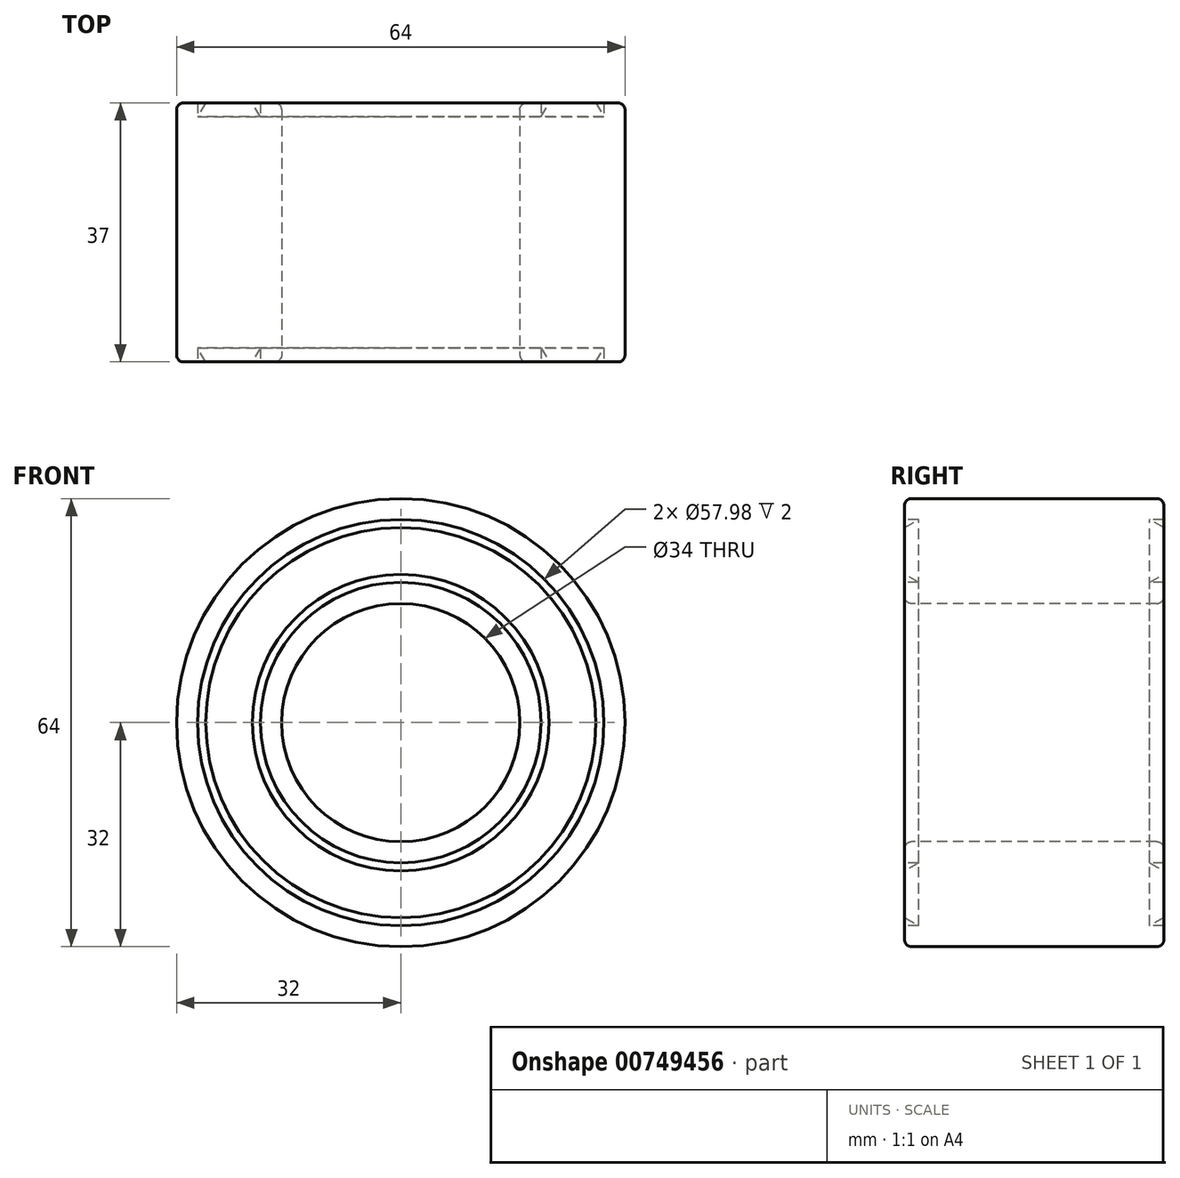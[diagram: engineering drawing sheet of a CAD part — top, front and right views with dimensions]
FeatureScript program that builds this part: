
annotation { "Feature Type Name" : "Feature", "Feature Type Description" : "" }
export const myFeature = defineFeature(function(context is Context, id is Id, definition is map)
    precondition{}
    {
        {
            var Q0;
            Q0=qCreatedBy(makeId("Right.planeOp"),FACE);
            var sketch = newSketch(context, id + "F0", { "sketchPlane" : qUnion([Q0])});
            skLineSegment(sketch, "E0", {"start": v(0, 17) * mm, "end": v(0, 20.03) * mm});
            skLineSegment(sketch, "E1", {"start": v(0, 20.03) * mm, "end": v(2, 20.03) * mm});
            skLineSegment(sketch, "E2", {"start": v(2, 20.03) * mm, "end": v(0, 21.18) * mm});
            skLineSegment(sketch, "E3", {"start": v(0, 21.18) * mm, "end": v(0, 27.83) * mm});
            skLineSegment(sketch, "E4", {"start": v(0, 27.83) * mm, "end": v(2, 28.99) * mm});
            skLineSegment(sketch, "E5", {"start": v(2, 28.99) * mm, "end": v(0, 28.99) * mm});
            skLineSegment(sketch, "E6", {"start": v(0, 28.99) * mm, "end": v(0, 32) * mm});
            skLineSegment(sketch, "E7", {"start": v(0, 32) * mm, "end": v(18.5, 32) * mm});
            skLineSegment(sketch, "E8", {"start": v(0, 17) * mm, "end": v(18.5, 17) * mm});
            skLineSegment(sketch, "E9", {"start": v(18.5, 17) * mm, "end": v(18.5, 32) * mm, "construction": true});
            skLineSegment(sketch, "E10.MirrorCS", {"start": v(37, 32) * mm, "end": v(18.5, 32) * mm});
            skLineSegment(sketch, "E11.MirrorCS", {"start": v(37, 28.99) * mm, "end": v(37, 32) * mm});
            skLineSegment(sketch, "E12.MirrorCS", {"start": v(35, 28.99) * mm, "end": v(37, 28.99) * mm});
            skLineSegment(sketch, "E13.MirrorCS", {"start": v(37, 27.83) * mm, "end": v(35, 28.99) * mm});
            skLineSegment(sketch, "E14.MirrorCS", {"start": v(37, 21.18) * mm, "end": v(37, 27.83) * mm});
            skLineSegment(sketch, "E15.MirrorCS", {"start": v(35, 20.03) * mm, "end": v(37, 21.18) * mm});
            skLineSegment(sketch, "E16.MirrorCS", {"start": v(37, 20.03) * mm, "end": v(35, 20.03) * mm});
            skLineSegment(sketch, "E17.MirrorCS", {"start": v(37, 17) * mm, "end": v(37, 20.03) * mm});
            skLineSegment(sketch, "E18.MirrorCS", {"start": v(37, 17) * mm, "end": v(18.5, 17) * mm});
            skLineSegment(sketch, "E19", {"start": v(0, 0) * mm, "end": v(4.54, 0) * mm, "construction": true});
            skSolve(sketch);
        }
        {
            var Q0;
            Q0 = qSketchRegion(id + "F0", true);
            var Q1;
            Q1=sQuery(id+"F0.wireOp",EDGE,"E19");
            revolve(context, id + "F1", {"surfaceOperationType" : NewSurfaceOperationType.NEW, "entities" : qUnion([Q0]), "axis" : qUnion([Q1]), "revolveType" : RevolveType.FULL});
        }
        {
            var Q0;
            Q0=makeQuery(id+"F1.opRevolve","SWEPT_EDGE",EDGE,{"disambiguationData":[OSD([sQuery(id+"F0.wireOp",EDGE,"E10.MirrorCS"),sQuery(id+"F0.wireOp",EDGE,"E11.MirrorCS")])]});
            var Q1;
            Q1=makeQuery(id+"F1.opRevolve","SWEPT_EDGE",EDGE,{"disambiguationData":[OSD([sQuery(id+"F0.wireOp",EDGE,"E17.MirrorCS"),sQuery(id+"F0.wireOp",EDGE,"E18.MirrorCS")])]});
            var Q2;
            Q2=makeQuery(id+"F1.opRevolve","SWEPT_FACE",FACE,{"disambiguationData":[OSD([sQuery(id+"F0.wireOp",EDGE,"E7"),sQuery(id+"F0.wireOp",EDGE,"E10.MirrorCS")])]});
            var Q3;
            Q3=makeQuery(id+"F1.opRevolve","SWEPT_EDGE",EDGE,{"disambiguationData":[OSD([sQuery(id+"F0.wireOp",EDGE,"E0"),sQuery(id+"F0.wireOp",EDGE,"E8")])]});
            fillet(context, id + "F2", {"entities" : qUnion([Q0, Q1, Q2, Q3]), "radius" : 1 * mm, "tangentPropagation" : true, "allowEdgeOverflow" : false});
        }
    });
